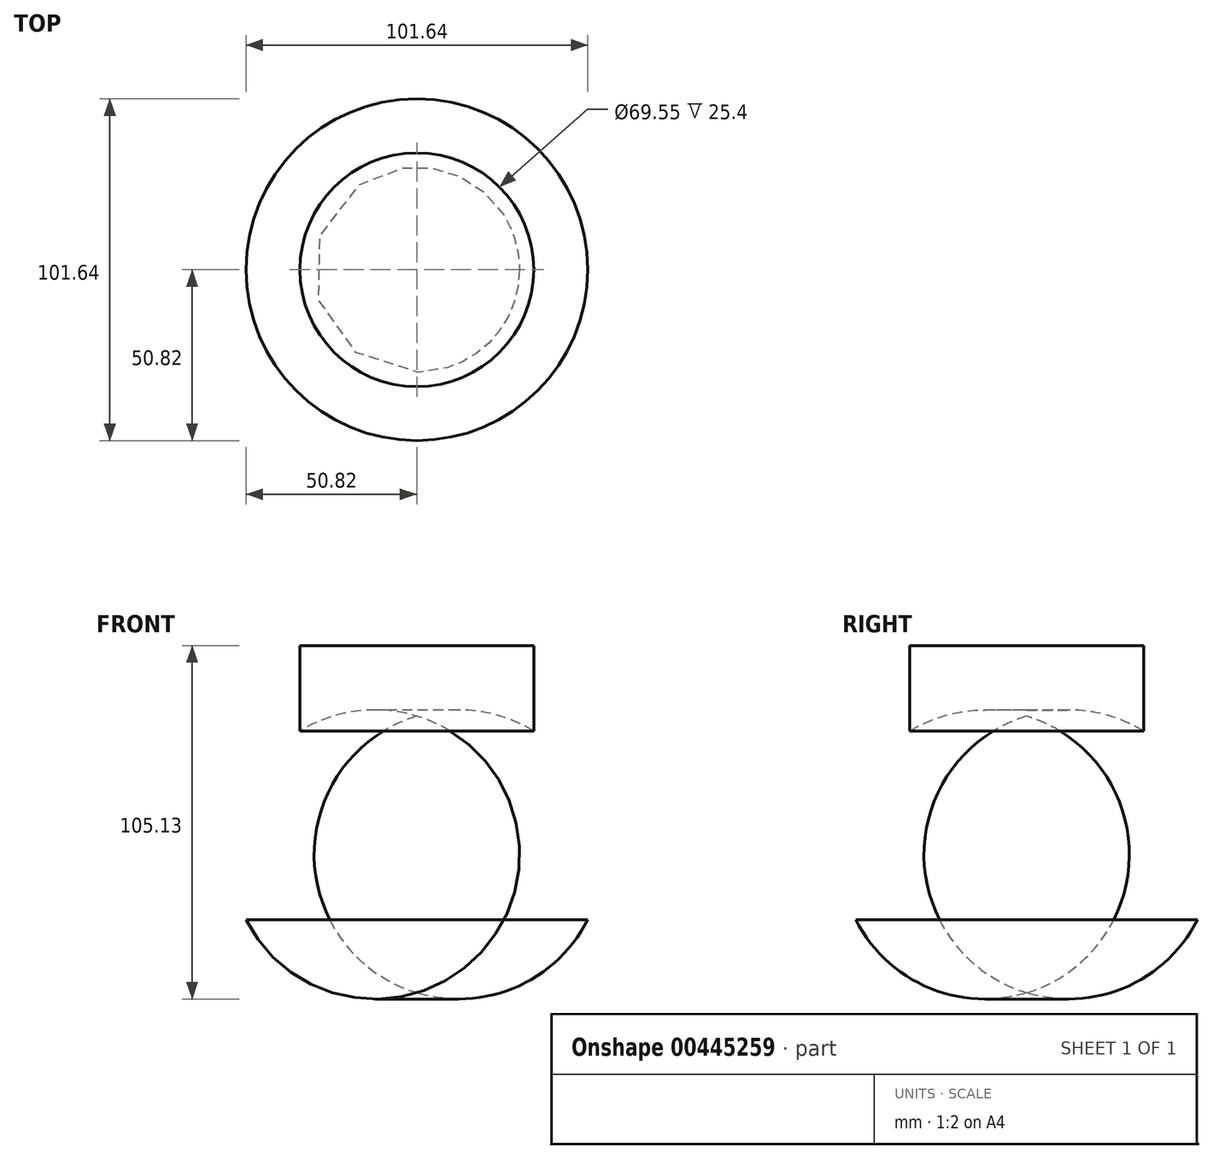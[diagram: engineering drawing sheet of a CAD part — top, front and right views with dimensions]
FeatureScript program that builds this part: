
annotation { "Feature Type Name" : "Feature", "Feature Type Description" : "" }
export const myFeature = defineFeature(function(context is Context, id is Id, definition is map)
    precondition{}
    {
        {
            var Q0;
            Q0=qCreatedBy(makeId("Right.planeOp"),FACE);
            var sketch = newSketch(context, id + "F0", { "sketchPlane" : qUnion([Q0])});
            skLineSegment(sketch, "E0", {"start": v(0, 0) * mm, "end": v(0, 28.48) * mm});
            skLineSegment(sketch, "E1", {"start": v(0, 28.48) * mm, "end": v(34.77, 28.48) * mm});
            skLineSegment(sketch, "E2", {"start": v(0, 0) * mm, "end": v(0, -27.66) * mm});
            skLineSegment(sketch, "E3", {"start": v(0, -27.66) * mm, "end": v(50.82, -27.66) * mm});
            skArc(sketch, "E4", {"start": v(50.82, -27.66) * mm, "mid": v(53.8, 3.55) * mm, "end": v(34.77, 28.48) * mm});
            skSolve(sketch);
        }
        {
            var Q0;
            Q0=makeQuery(id+"F0.imprint","IMPRINT",FACE,{"disambiguationData":[TD([[makeQuery(id+"F0.imprint","IMPRINT",EDGE,{"derivedFrom":sQuery(id+"F0.wireOp",EDGE,"E0")}),-1.0]])]});
            var Q1;
            Q1=sQuery(id+"F0.wireOp",EDGE,"E0");
            revolve(context, id + "F1", {"entities" : qUnion([Q0]), "axis" : qUnion([Q1]), "revolveType" : RevolveType.FULL});
        }
        {
            var Q0;
            Q0=makeQuery(id+"F1.opRevolve","SWEPT_FACE",FACE,{"disambiguationData":[OSD([sQuery(id+"F0.wireOp",EDGE,"E1")])]});
            extrude(context, id + "F2", {"entities" : qUnion([Q0]), "operationType" : NewBodyOperationType.ADD, "depth" : 25.4 * mm});
        }
    });
